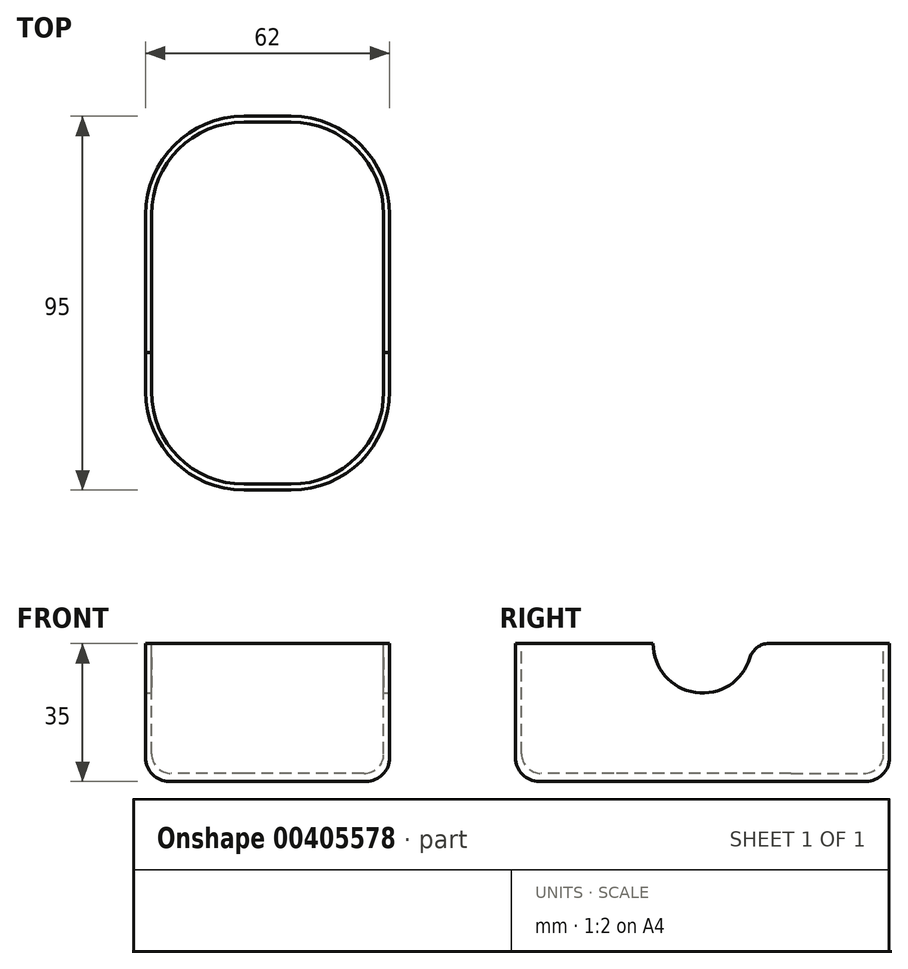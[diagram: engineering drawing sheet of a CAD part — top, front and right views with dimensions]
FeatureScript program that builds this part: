
annotation { "Feature Type Name" : "Feature", "Feature Type Description" : "" }
export const myFeature = defineFeature(function(context is Context, id is Id, definition is map)
    precondition{}
    {
        {
            var Q0;
            Q0=qCreatedBy(makeId("Top.planeOp"),FACE);
            var sketch = newSketch(context, id + "F0", { "sketchPlane" : qUnion([Q0])});
            skLineSegment(sketch, "E0.bottom", {"start": v(31, 47.5) * mm, "end": v(-31, 47.5) * mm});
            skLineSegment(sketch, "E0.top", {"start": v(31, -47.5) * mm, "end": v(-31, -47.5) * mm});
            skLineSegment(sketch, "E0.left", {"start": v(31, 47.5) * mm, "end": v(31, -47.5) * mm});
            skLineSegment(sketch, "E0.right", {"start": v(-31, 47.5) * mm, "end": v(-31, -47.5) * mm});
            skPoint(sketch, "E0.middle", {"position": v(0, 0) * mm});
            skSolve(sketch);
        }
        {
            var Q0;
            Q0=makeQuery(id+"F0.imprint","IMPRINT",FACE,{"disambiguationData":[TD([[makeQuery(id+"F0.imprint","IMPRINT",EDGE,{"derivedFrom":sQuery(id+"F0.wireOp",EDGE,"E0.bottom")}),1.0]])]});
            extrude(context, id + "F1", {"entities" : qUnion([Q0]), "depth" : 35 * mm});
        }
        {
            var Q0;
            Q0=makeQuery(id+"F1.opExtrude","SWEPT_EDGE",EDGE,{"disambiguationData":[OSD([sQuery(id+"F0.wireOp",EDGE,"E0.bottom"),sQuery(id+"F0.wireOp",EDGE,"E0.left")])]});
            var Q1;
            Q1=makeQuery(id+"F1.opExtrude","SWEPT_EDGE",EDGE,{"disambiguationData":[OSD([sQuery(id+"F0.wireOp",EDGE,"E0.bottom"),sQuery(id+"F0.wireOp",EDGE,"E0.right")])]});
            var Q2;
            Q2=makeQuery(id+"F1.opExtrude","SWEPT_EDGE",EDGE,{"disambiguationData":[OSD([sQuery(id+"F0.wireOp",EDGE,"E0.top"),sQuery(id+"F0.wireOp",EDGE,"E0.left")])]});
            var Q3;
            Q3=makeQuery(id+"F1.opExtrude","SWEPT_EDGE",EDGE,{"disambiguationData":[OSD([sQuery(id+"F0.wireOp",EDGE,"E0.top"),sQuery(id+"F0.wireOp",EDGE,"E0.right")])]});
            fillet(context, id + "F2", {"entities" : qUnion([Q0, Q1, Q2, Q3]), "radius" : 25 * mm, "tangentPropagation" : true, "allowEdgeOverflow" : false});
        }
        {
            var Q0;
            Q0=makeQuery(id+"F1.opExtrude","CAP_FACE",FACE,{"disambiguationData":[OSD([sQuery(id+"F0.wireOp",EDGE,"E0.bottom"),sQuery(id+"F0.wireOp",EDGE,"E0.top"),sQuery(id+"F0.wireOp",EDGE,"E0.left"),sQuery(id+"F0.wireOp",EDGE,"E0.right")])],"isStart":false});
            var sketch = newSketch(context, id + "F3", { "sketchPlane" : qUnion([Q0])});
            skArc(sketch, "E1.0", {"start": v(29.5, 22.5) * mm, "mid": v(22.62, 39.12) * mm, "end": v(6, 46) * mm});
            skLineSegment(sketch, "E1.1", {"start": v(6, 46) * mm, "end": v(-6, 46) * mm});
            skLineSegment(sketch, "E1.2", {"start": v(29.5, 22.5) * mm, "end": v(29.5, -22.5) * mm});
            skArc(sketch, "E1.3", {"start": v(-6, 46) * mm, "mid": v(-22.62, 39.12) * mm, "end": v(-29.5, 22.5) * mm});
            skArc(sketch, "E1.4", {"start": v(6, -46) * mm, "mid": v(22.62, -39.12) * mm, "end": v(29.5, -22.5) * mm});
            skLineSegment(sketch, "E1.5", {"start": v(6, -46) * mm, "end": v(-6, -46) * mm});
            skArc(sketch, "E1.6", {"start": v(-29.5, -22.5) * mm, "mid": v(-22.62, -39.12) * mm, "end": v(-6, -46) * mm});
            skLineSegment(sketch, "E1.7", {"start": v(-29.5, 22.5) * mm, "end": v(-29.5, -22.5) * mm});
            skSolve(sketch);
        }
        {
            var Q0;
            Q0=makeQuery(id+"F3.imprint","IMPRINT",FACE,{"disambiguationData":[TD([[makeQuery(id+"F3.imprint","IMPRINT",EDGE,{"derivedFrom":sQuery(id+"F3.wireOp",EDGE,"E1.0")}),1.0]])]});
            extrude(context, id + "F4", {"entities" : qUnion([Q0]), "operationType" : NewBodyOperationType.REMOVE, "oppositeDirection" : true, "depth" : 33 * mm});
        }
        {
            var Q0;
            Q0=makeQuery(id+"F1.opExtrude","SWEPT_FACE",FACE,{"disambiguationData":[OSD([sQuery(id+"F0.wireOp",EDGE,"E0.left")])]});
            var sketch = newSketch(context, id + "F5", { "sketchPlane" : qUnion([Q0])});
            skCircle(sketch, "E2", {"center": v(0, 35) * mm, "radius": 12.57 * mm});
            skSolve(sketch);
        }
        {
            var Q0;
            {var subQ0=sQuery(id+"F5.wireOp",EDGE,"E2");var subQ1=makeQuery(id+"F1.opExtrude","CAP_EDGE",EDGE,{"disambiguationData":[OSD([sQuery(id+"F0.wireOp",EDGE,"E0.left")])],"isStart":false});var subQ2=makeQuery(id+"F5.imprint","INTERSECT",VERTEX,{"disambiguationData":[OD(0.0)],"derivedFrom":[subQ1,subQ0]});Q0=makeQuery(id+"F5.imprint","IMPRINT",FACE,{"disambiguationData":[TD([[makeQuery(id+"F5.imprint","IMPRINT",EDGE,{"disambiguationData":[TD([[subQ2,1.0]])],"derivedFrom":subQ0}),1.0]])]});}
            var Q1;
            Q1=sQuery(id+"F5.wireOp",EDGE,"E2");
            extrude(context, id + "F6", {"entities" : qUnion([Q0]), "operationType" : NewBodyOperationType.REMOVE, "surfaceEntities" : qUnion([Q1]), "endBound" : BoundingType.THROUGH_ALL, "oppositeDirection" : true, "depth" : 25 * mm});
        }
        {
            var Q0;
            {var subQ0=sQuery(id+"F0.wireOp",EDGE,"E0.left");var subQ1=sQuery(id+"F5.wireOp",EDGE,"E2");Q0=makeQuery(id+"F6.boolean.opBoolean","COPY",EDGE,{"disambiguationData":[TD([makeQuery(id+"F1.opExtrude","SWEPT_FACE",FACE,{"disambiguationData":[OSD([subQ0])]})])],"derivedFrom":makeQuery(id+"F6.opExtrude","SWEPT_EDGE",EDGE,{"disambiguationData":[OSD([subQ0,subQ1]),TDD([makeQuery(id+"F5.imprint","INTERSECT",VERTEX,{"disambiguationData":[OD(0.0)],"derivedFrom":[makeQuery(id+"F1.opExtrude","CAP_EDGE",EDGE,{"disambiguationData":[OSD([subQ0])],"isStart":false}),subQ1]})])]})});}
            var Q1;
            {var subQ0=sQuery(id+"F0.wireOp",EDGE,"E0.right");var subQ1=sQuery(id+"F0.wireOp",EDGE,"E0.left");var subQ2=sQuery(id+"F5.wireOp",EDGE,"E2");Q1=makeQuery(id+"F6.boolean.opBoolean","COPY",EDGE,{"disambiguationData":[TD([makeQuery(id+"F1.opExtrude","SWEPT_FACE",FACE,{"disambiguationData":[OSD([subQ0])]})])],"derivedFrom":makeQuery(id+"F6.opExtrude","SWEPT_EDGE",EDGE,{"disambiguationData":[OSD([subQ1,subQ2]),TDD([makeQuery(id+"F5.imprint","INTERSECT",VERTEX,{"disambiguationData":[OD(0.0)],"derivedFrom":[makeQuery(id+"F1.opExtrude","CAP_EDGE",EDGE,{"disambiguationData":[OSD([subQ1])],"isStart":false}),subQ2]})])]})});}
            var Q2;
            {var subQ0=sQuery(id+"F0.wireOp",EDGE,"E0.left");var subQ1=sQuery(id+"F5.wireOp",EDGE,"E2");Q2=makeQuery(id+"F6.boolean.opBoolean","COPY",EDGE,{"disambiguationData":[TD([makeQuery(id+"F1.opExtrude","SWEPT_FACE",FACE,{"disambiguationData":[OSD([subQ0])]})])],"derivedFrom":makeQuery(id+"F6.opExtrude","SWEPT_EDGE",EDGE,{"disambiguationData":[OSD([subQ0,subQ1]),TDD([makeQuery(id+"F5.imprint","INTERSECT",VERTEX,{"disambiguationData":[OD(1.0)],"derivedFrom":[makeQuery(id+"F1.opExtrude","CAP_EDGE",EDGE,{"disambiguationData":[OSD([subQ0])],"isStart":false}),subQ1]})])]})});}
            var Q3;
            {var subQ0=sQuery(id+"F0.wireOp",EDGE,"E0.right");var subQ1=sQuery(id+"F0.wireOp",EDGE,"E0.left");var subQ2=sQuery(id+"F5.wireOp",EDGE,"E2");Q3=makeQuery(id+"F6.boolean.opBoolean","COPY",EDGE,{"disambiguationData":[TD([makeQuery(id+"F1.opExtrude","SWEPT_FACE",FACE,{"disambiguationData":[OSD([subQ0])]})])],"derivedFrom":makeQuery(id+"F6.opExtrude","SWEPT_EDGE",EDGE,{"disambiguationData":[OSD([subQ1,subQ2]),TDD([makeQuery(id+"F5.imprint","INTERSECT",VERTEX,{"disambiguationData":[OD(1.0)],"derivedFrom":[makeQuery(id+"F1.opExtrude","CAP_EDGE",EDGE,{"disambiguationData":[OSD([subQ1])],"isStart":false}),subQ2]})])]})});}
            fillet(context, id + "F7", {"entities" : qUnion([Q0, Q1, Q2, Q3]), "radius" : 5 * mm, "tangentPropagation" : true, "allowEdgeOverflow" : false});
        }
        {
            var Q0;
            Q0=makeQuery(id+"F4.boolean.opBoolean","COPY",EDGE,{"derivedFrom":makeQuery(id+"F4.opExtrude","CAP_EDGE",EDGE,{"disambiguationData":[OSD([sQuery(id+"F3.wireOp",EDGE,"E1.3")])],"isStart":false})});
            fillet(context, id + "F8", {"entities" : qUnion([Q0]), "radius" : 5 * mm, "tangentPropagation" : true, "allowEdgeOverflow" : false});
        }
        {
            var Q0;
            Q0=makeQuery(id+"F1.opExtrude","CAP_EDGE",EDGE,{"disambiguationData":[OSD([sQuery(id+"F0.wireOp",EDGE,"E0.left")])],"isStart":true});
            fillet(context, id + "F9", {"entities" : qUnion([Q0]), "radius" : 6 * mm, "tangentPropagation" : true, "allowEdgeOverflow" : false});
        }
    });
